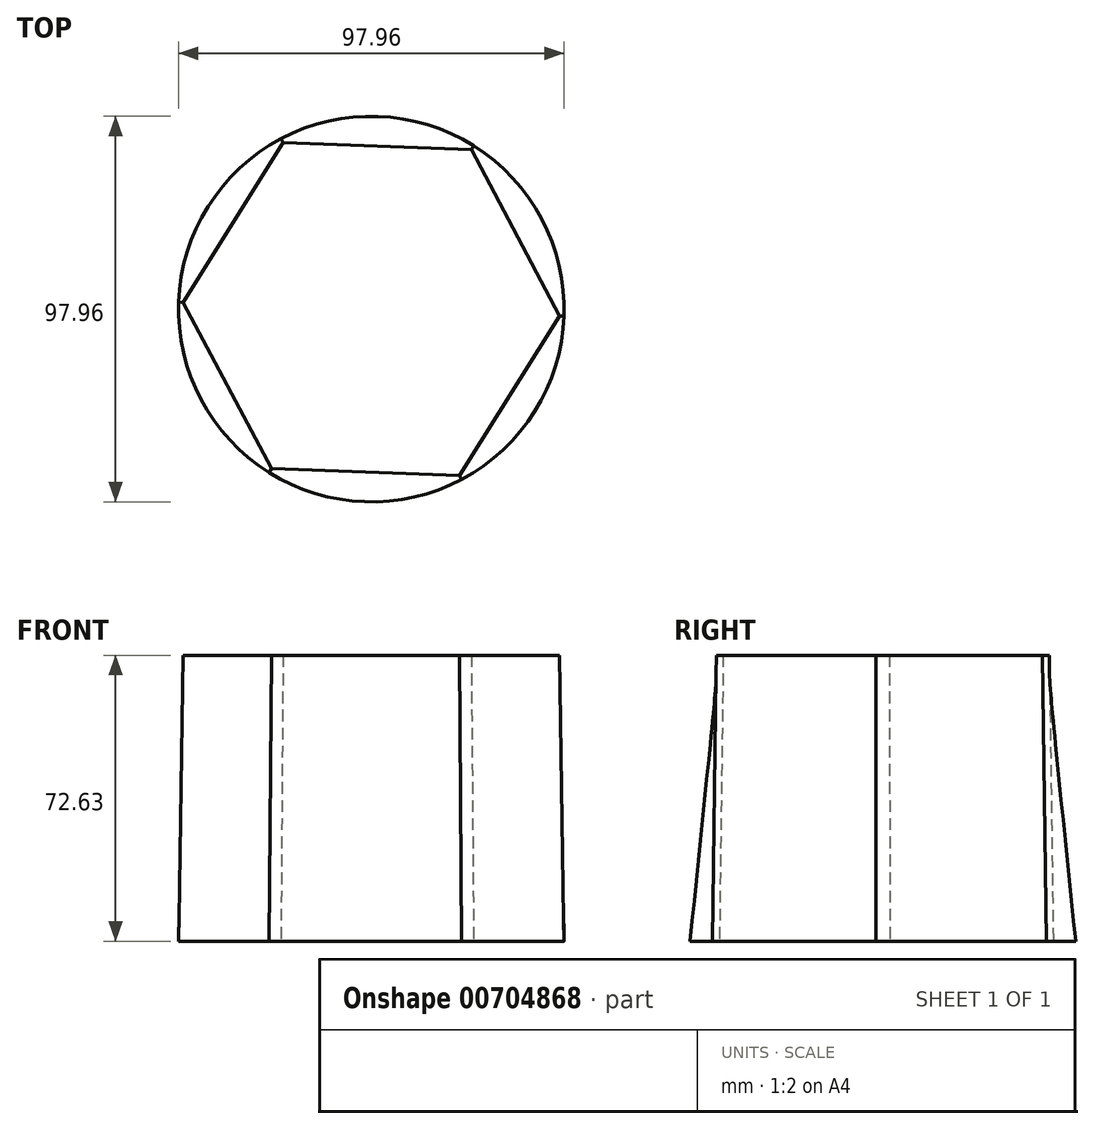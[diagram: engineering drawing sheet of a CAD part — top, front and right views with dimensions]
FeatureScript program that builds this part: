
annotation { "Feature Type Name" : "Feature", "Feature Type Description" : "" }
export const myFeature = defineFeature(function(context is Context, id is Id, definition is map)
    precondition{}
    {
        {
            var Q0;
            Q0=qCreatedBy(makeId("Top.planeOp"),FACE);
            var sketch = newSketch(context, id + "F0", { "sketchPlane" : qUnion([Q0])});
            skCircle(sketch, "E0", {"center": v(0, 0) * mm, "radius": 48.98 * mm});
            skSolve(sketch);
        }
        {
            var Q0;
            Q0=qCreatedBy(makeId("Top.planeOp"),FACE);
            cPlane(context, id + "F1", {"entities" : qUnion([Q0]), "cplaneType" : CPlaneType.OFFSET, "offset" : 72.63 * mm, "width" : 150 * mm, "height" : 150 * mm});
        }
        {
            var Q0;
            Q0=qCreatedBy(id+"F1.planeOp",FACE);
            var sketch = newSketch(context, id + "F2", { "sketchPlane" : qUnion([Q0])});
            skCircle(sketch, "E1.cCircle", {"center": v(0, 0) * mm, "radius": 41.45 * mm, "construction": true});
            skLineSegment(sketch, "E1.0", {"start": v(47.83, -1.71) * mm, "end": v(22.43, -42.28) * mm});
            skLineSegment(sketch, "E1.1", {"start": v(22.43, -42.28) * mm, "end": v(-25.4, -40.57) * mm});
            skLineSegment(sketch, "E1.2", {"start": v(-25.4, -40.57) * mm, "end": v(-47.83, 1.71) * mm});
            skLineSegment(sketch, "E1.3", {"start": v(-47.83, 1.71) * mm, "end": v(-22.43, 42.28) * mm});
            skLineSegment(sketch, "E1.4", {"start": v(-22.43, 42.28) * mm, "end": v(25.4, 40.57) * mm});
            skLineSegment(sketch, "E1.5", {"start": v(25.4, 40.57) * mm, "end": v(47.83, -1.71) * mm});
            skPoint(sketch, "E1.0.midPoint", {"position": v(35.13, -22) * mm});
            skSolve(sketch);
        }
        {
            var Q0;
            Q0=makeQuery(id+"F2.imprint","IMPRINT",FACE,{"disambiguationData":[TD([[makeQuery(id+"F2.imprint","IMPRINT",EDGE,{"derivedFrom":sQuery(id+"F2.wireOp",EDGE,"E1.0")}),-1.0]])]});
            var Q1;
            Q1=makeQuery(id+"F0.imprint","IMPRINT",FACE,{"disambiguationData":[TD([[makeQuery(id+"F0.imprint","IMPRINT",EDGE,{"derivedFrom":sQuery(id+"F0.wireOp",EDGE,"E0")}),1.0]])]});
            loft(context, id + "F3", {"sheetProfilesArray" : [{ "sheetProfileEntities" : qUnion([Q0]) }, { "sheetProfileEntities" : qUnion([Q1]) }]});
        }
    });
